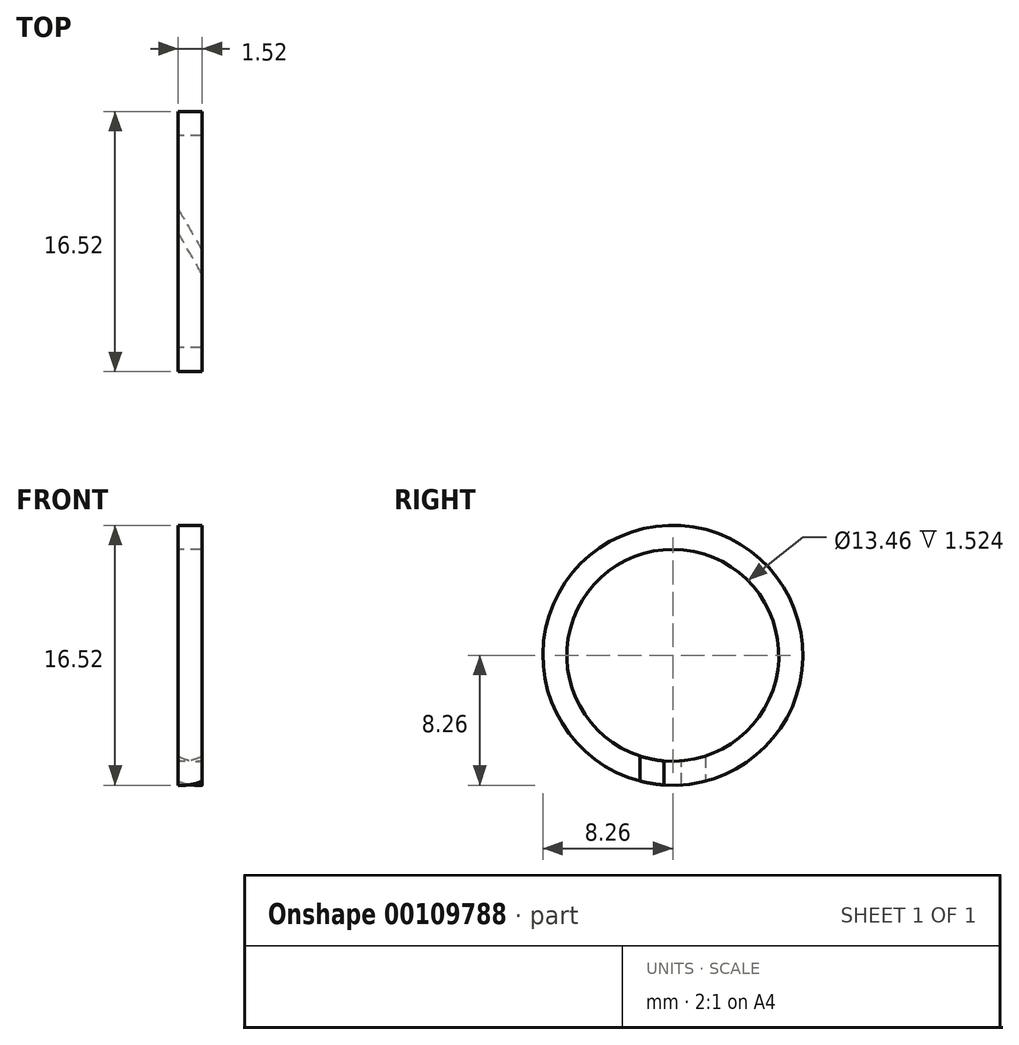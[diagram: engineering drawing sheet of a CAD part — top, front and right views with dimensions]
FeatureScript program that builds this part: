
annotation { "Feature Type Name" : "Feature", "Feature Type Description" : "" }
export const myFeature = defineFeature(function(context is Context, id is Id, definition is map)
    precondition{}
    {
        {
            var Q0;
            Q0=qCreatedBy(makeId("Right.planeOp"),FACE);
            var sketch = newSketch(context, id + "F0", { "sketchPlane" : qUnion([Q0])});
            skCircle(sketch, "E0", {"center": v(0, 0) * mm, "radius": 6.73 * mm});
            skCircle(sketch, "E1", {"center": v(0, 0) * mm, "radius": 8.26 * mm});
            skSolve(sketch);
        }
        {
            var Q0;
            Q0 = qSketchRegion(id + "F0", true);
            extrude(context, id + "F1", {"entities" : qUnion([Q0]), "endBound" : BoundingType.SYMMETRIC, "depth" : 1.52 * mm});
        }
        {
            var Q0;
            Q0=qCreatedBy(makeId("Top.planeOp"),FACE);
            var sketch = newSketch(context, id + "F2", { "sketchPlane" : qUnion([Q0])});
            skLineSegment(sketch, "E2", {"start": v(0.91, -2.35) * mm, "end": v(-0.88, 0.75) * mm});
            skLineSegment(sketch, "E3", {"start": v(-1.06, 2.6) * mm, "end": v(1.27, -1.43) * mm});
            skLineSegment(sketch, "E4", {"start": v(0.91, -2.35) * mm, "end": v(1.27, -1.43) * mm});
            skLineSegment(sketch, "E5", {"start": v(-0.88, 0.75) * mm, "end": v(-1.06, 2.6) * mm});
            skSolve(sketch);
        }
        {
            var Q0;
            Q0 = qSketchRegion(id + "F2", true);
            extrude(context, id + "F3", {"entities" : qUnion([Q0]), "operationType" : NewBodyOperationType.REMOVE, "oppositeDirection" : true, "depth" : 25.4 * mm});
        }
    });
